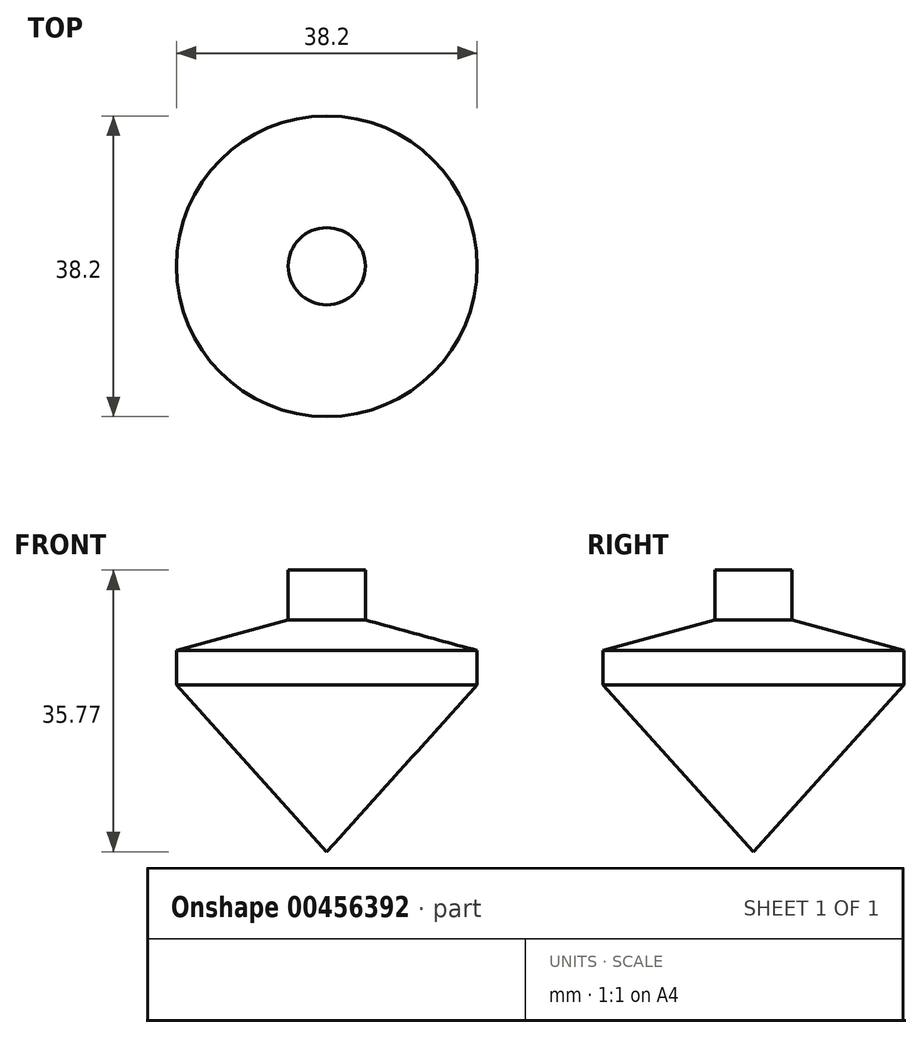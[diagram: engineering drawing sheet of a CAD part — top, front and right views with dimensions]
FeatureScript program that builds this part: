
annotation { "Feature Type Name" : "Feature", "Feature Type Description" : "" }
export const myFeature = defineFeature(function(context is Context, id is Id, definition is map)
    precondition{}
    {
        {
            var Q0;
            Q0=qCreatedBy(makeId("Front.planeOp"),FACE);
            var sketch = newSketch(context, id + "F0", { "sketchPlane" : qUnion([Q0])});
            skLineSegment(sketch, "E0", {"start": v(0, 0) * mm, "end": v(19.1, 21.16) * mm});
            skLineSegment(sketch, "E1", {"start": v(19.1, 21.16) * mm, "end": v(19.1, 25.55) * mm});
            skLineSegment(sketch, "E2", {"start": v(19.1, 25.55) * mm, "end": v(4.9, 29.42) * mm});
            skLineSegment(sketch, "E3", {"start": v(4.9, 29.42) * mm, "end": v(0, 29.42) * mm});
            skLineSegment(sketch, "E4", {"start": v(0, 29.42) * mm, "end": v(0, 0) * mm});
            skSolve(sketch);
        }
        {
            var Q0;
            Q0=makeQuery(id+"F0.imprint","IMPRINT",FACE,{"disambiguationData":[TD([[makeQuery(id+"F0.imprint","IMPRINT",EDGE,{"derivedFrom":sQuery(id+"F0.wireOp",EDGE,"E0")}),1.0]])]});
            var Q1;
            Q1=sQuery(id+"F0.wireOp",EDGE,"E4");
            revolve(context, id + "F1", {"entities" : qUnion([Q0]), "axis" : qUnion([Q1]), "revolveType" : RevolveType.FULL});
        }
        {
            var Q0;
            Q0=makeQuery(id+"F1.opRevolve","SWEPT_FACE",FACE,{"disambiguationData":[OSD([sQuery(id+"F0.wireOp",EDGE,"E3")])]});
            extrude(context, id + "F2", {"entities" : qUnion([Q0]), "operationType" : NewBodyOperationType.ADD, "depth" : 6.35 * mm});
        }
        {
            var Q0;
            Q0=makeQuery(id+"F2.opExtrude","CAP_FACE",FACE,{"disambiguationData":[OSD([sQuery(id+"F0.wireOp",EDGE,"E3")])],"isStart":false});
            var sketch = newSketch(context, id + "F3", { "sketchPlane" : qUnion([Q0])});
            skCircle(sketch, "E5", {"center": v(0, 0) * mm, "radius": 2.53 * mm});
            skSolve(sketch);
        }
        {
            var Q0;
            Q0=sQuery(id+"F3.wireOp",EDGE,"E5");
            extrude(context, id + "F4", {"bodyType" : ToolBodyType.SURFACE, "surfaceEntities" : qUnion([Q0]), "depth" : -25.4 * mm});
        }
    });
